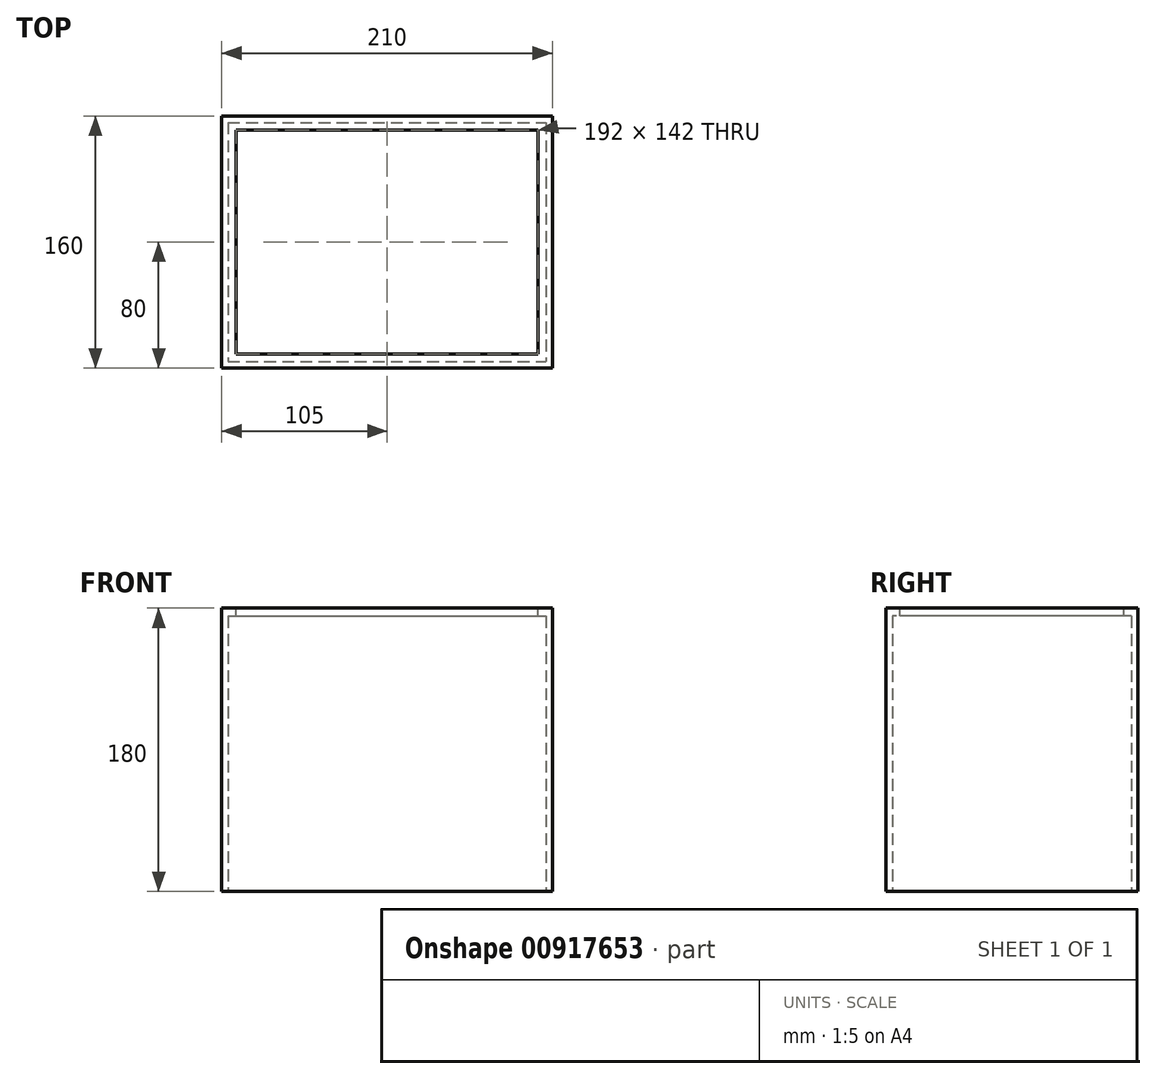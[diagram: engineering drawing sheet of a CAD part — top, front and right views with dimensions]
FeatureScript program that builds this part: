
annotation { "Feature Type Name" : "Feature", "Feature Type Description" : "" }
export const myFeature = defineFeature(function(context is Context, id is Id, definition is map)
    precondition{}
    {
        {
            var Q0;
            Q0=qCreatedBy(makeId("Top.planeOp"),FACE);
            var sketch = newSketch(context, id + "F0", { "sketchPlane" : qUnion([Q0])});
            skLineSegment(sketch, "E0.bottom", {"start": v(-105, 80) * mm, "end": v(105, 80) * mm});
            skLineSegment(sketch, "E0.top", {"start": v(-105, -80) * mm, "end": v(105, -80) * mm});
            skLineSegment(sketch, "E0.left", {"start": v(-105, 80) * mm, "end": v(-105, -80) * mm});
            skLineSegment(sketch, "E0.right", {"start": v(105, 80) * mm, "end": v(105, -80) * mm});
            skPoint(sketch, "E0.middle", {"position": v(0, 0) * mm});
            skSolve(sketch);
        }
        {
            var Q0;
            Q0=makeQuery(id+"F0.imprint","IMPRINT",FACE,{"disambiguationData":[TD([[makeQuery(id+"F0.imprint","IMPRINT",EDGE,{"derivedFrom":sQuery(id+"F0.wireOp",EDGE,"E0.bottom")}),-1.0]])]});
            extrude(context, id + "F1", {"entities" : qUnion([Q0]), "depth" : 180 * mm, "offsetDistance" : 25 * mm});
        }
        {
            var Q0;
            Q0=makeQuery(id+"F1.opExtrude","CAP_FACE",FACE,{"disambiguationData":[OSD([sQuery(id+"F0.wireOp",EDGE,"E0.bottom"),sQuery(id+"F0.wireOp",EDGE,"E0.top"),sQuery(id+"F0.wireOp",EDGE,"E0.left"),sQuery(id+"F0.wireOp",EDGE,"E0.right")])],"isStart":false});
            var Q1;
            Q1=makeQuery(id+"F1.opExtrude","CAP_FACE",FACE,{"disambiguationData":[OSD([sQuery(id+"F0.wireOp",EDGE,"E0.bottom"),sQuery(id+"F0.wireOp",EDGE,"E0.top"),sQuery(id+"F0.wireOp",EDGE,"E0.left"),sQuery(id+"F0.wireOp",EDGE,"E0.right")])],"isStart":true});
            shell(context, id + "F2", {"entities" : qUnion([Q0, Q1]), "thickness" : 4 * mm});
        }
        {
            var Q0;
            Q0=makeQuery(id+"F1.opExtrude","CAP_FACE",FACE,{"disambiguationData":[OSD([sQuery(id+"F0.wireOp",EDGE,"E0.bottom"),sQuery(id+"F0.wireOp",EDGE,"E0.top"),sQuery(id+"F0.wireOp",EDGE,"E0.left"),sQuery(id+"F0.wireOp",EDGE,"E0.right")])],"isStart":false});
            var sketch = newSketch(context, id + "F3", { "sketchPlane" : qUnion([Q0])});
            skLineSegment(sketch, "E1.0", {"start": v(96, 71) * mm, "end": v(96, -71) * mm});
            skLineSegment(sketch, "E1.1", {"start": v(-96, 71) * mm, "end": v(96, 71) * mm});
            skLineSegment(sketch, "E1.2", {"start": v(-96, 71) * mm, "end": v(-96, -71) * mm});
            skLineSegment(sketch, "E1.3", {"start": v(-96, -71) * mm, "end": v(96, -71) * mm});
            skLineSegment(sketch, "E2.0", {"start": v(-105, 80) * mm, "end": v(105, 80) * mm});
            skLineSegment(sketch, "E2.1", {"start": v(-105, 80) * mm, "end": v(-105, -80) * mm});
            skLineSegment(sketch, "E2.2", {"start": v(-105, -80) * mm, "end": v(105, -80) * mm});
            skLineSegment(sketch, "E2.3", {"start": v(105, 80) * mm, "end": v(105, -80) * mm});
            skSolve(sketch);
        }
        {
            var Q0;
            Q0 = qSketchRegion(id + "F3", true);
            extrude(context, id + "F4", {"entities" : qUnion([Q0]), "operationType" : NewBodyOperationType.ADD, "oppositeDirection" : true, "depth" : 5 * mm, "offsetDistance" : 25 * mm});
        }
    });
